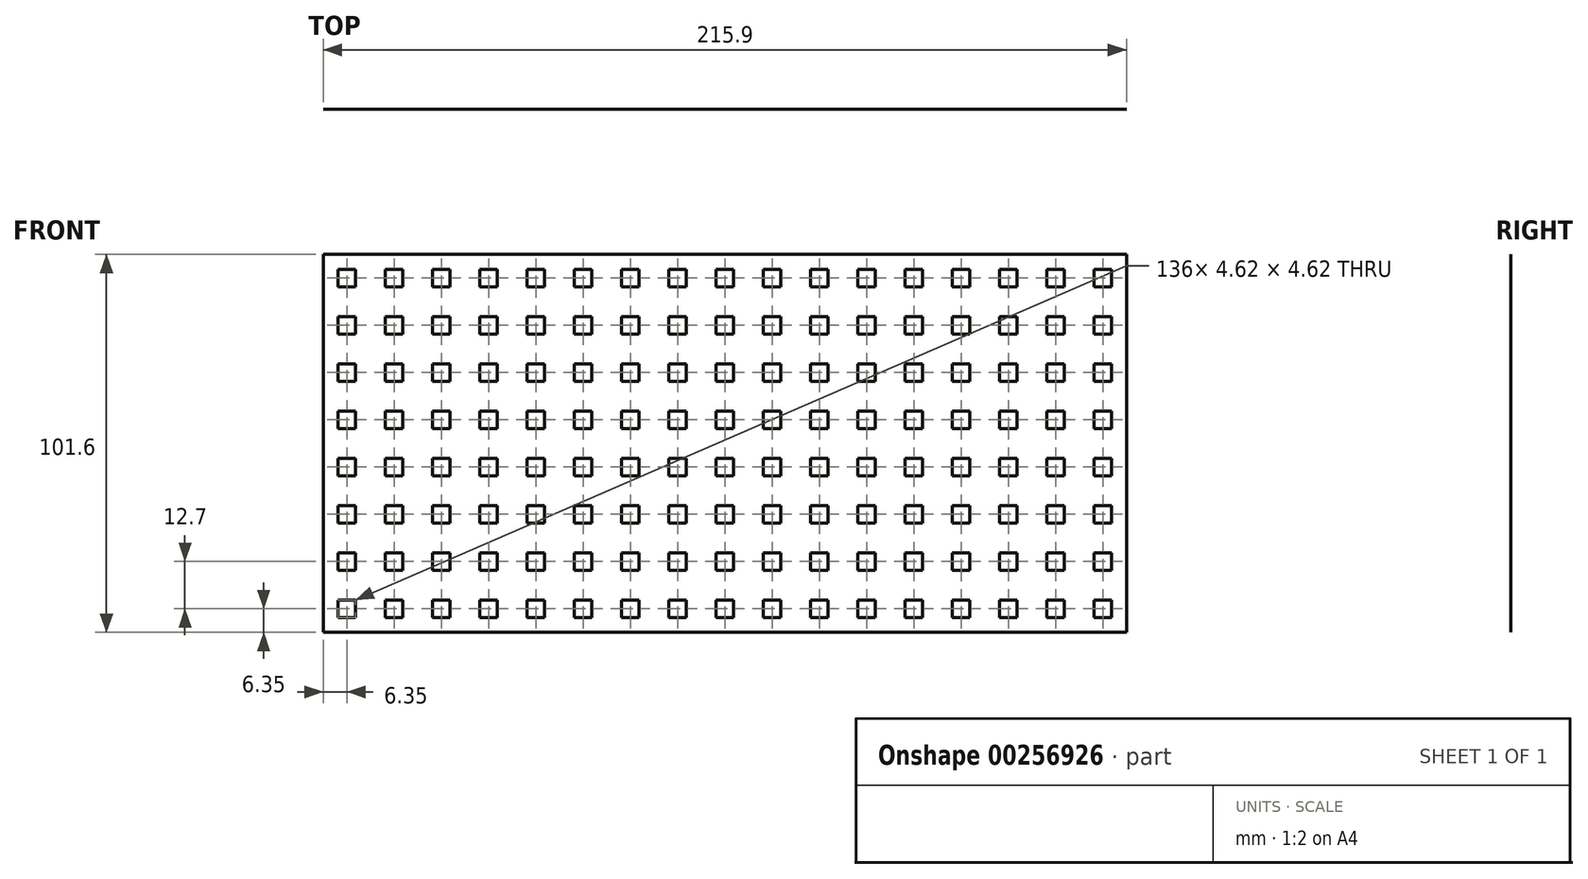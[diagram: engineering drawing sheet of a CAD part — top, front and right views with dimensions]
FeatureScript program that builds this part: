
annotation { "Feature Type Name" : "Feature", "Feature Type Description" : "" }
export const myFeature = defineFeature(function(context is Context, id is Id, definition is map)
    precondition{}
    {
        {
            var Q0;
            Q0=qCreatedBy(makeId("Front.planeOp"),FACE);
            var sketch = newSketch(context, id + "F0", { "sketchPlane" : qUnion([Q0])});
            skLineSegment(sketch, "E0.bottom", {"start": v(107.95, 50.8) * mm, "end": v(-107.95, 50.8) * mm});
            skLineSegment(sketch, "E0.top", {"start": v(107.95, -50.8) * mm, "end": v(-107.95, -50.8) * mm});
            skLineSegment(sketch, "E0.left", {"start": v(107.95, 50.8) * mm, "end": v(107.95, -50.8) * mm});
            skLineSegment(sketch, "E0.right", {"start": v(-107.95, 50.8) * mm, "end": v(-107.95, -50.8) * mm});
            skPoint(sketch, "E0.middle", {"position": v(0, 0) * mm});
            skLineSegment(sketch, "E1.bottom", {"start": v(-107.95, -50.8) * mm, "end": v(-101.6, -50.8) * mm});
            skLineSegment(sketch, "E1.left", {"start": v(-107.95, -50.8) * mm, "end": v(-107.95, -44.45) * mm});
            skLineSegment(sketch, "E2.bottom", {"start": v(-99.29, -46.76) * mm, "end": v(-103.91, -46.76) * mm});
            skLineSegment(sketch, "E2.top", {"start": v(-99.29, -42.14) * mm, "end": v(-103.91, -42.14) * mm});
            skLineSegment(sketch, "E2.left", {"start": v(-99.29, -46.76) * mm, "end": v(-99.29, -42.14) * mm});
            skLineSegment(sketch, "E2.right", {"start": v(-103.91, -46.76) * mm, "end": v(-103.91, -42.14) * mm});
            skPoint(sketch, "E2.middle", {"position": v(-101.6, -44.45) * mm});
            skLineSegment(sketch, "E3.0.1.0", {"start": v(-99.29, -29.44) * mm, "end": v(-103.91, -29.44) * mm});
            skLineSegment(sketch, "E3.0.1.1", {"start": v(-103.91, -34.06) * mm, "end": v(-103.91, -29.44) * mm});
            skLineSegment(sketch, "E3.0.1.2", {"start": v(-99.29, -34.06) * mm, "end": v(-103.91, -34.06) * mm});
            skLineSegment(sketch, "E3.0.1.3", {"start": v(-99.29, -34.06) * mm, "end": v(-99.29, -29.44) * mm});
            skLineSegment(sketch, "E3.0.2.0", {"start": v(-99.29, -16.74) * mm, "end": v(-103.91, -16.74) * mm});
            skLineSegment(sketch, "E3.0.2.1", {"start": v(-103.91, -21.36) * mm, "end": v(-103.91, -16.74) * mm});
            skLineSegment(sketch, "E3.0.2.2", {"start": v(-99.29, -21.36) * mm, "end": v(-103.91, -21.36) * mm});
            skLineSegment(sketch, "E3.0.2.3", {"start": v(-99.29, -21.36) * mm, "end": v(-99.29, -16.74) * mm});
            skLineSegment(sketch, "E3.0.3.0", {"start": v(-99.29, -4.04) * mm, "end": v(-103.91, -4.04) * mm});
            skLineSegment(sketch, "E3.0.3.1", {"start": v(-103.91, -8.66) * mm, "end": v(-103.91, -4.04) * mm});
            skLineSegment(sketch, "E3.0.3.2", {"start": v(-99.29, -8.66) * mm, "end": v(-103.91, -8.66) * mm});
            skLineSegment(sketch, "E3.0.3.3", {"start": v(-99.29, -8.66) * mm, "end": v(-99.29, -4.04) * mm});
            skLineSegment(sketch, "E3.0.4.0", {"start": v(-99.29, 8.66) * mm, "end": v(-103.91, 8.66) * mm});
            skLineSegment(sketch, "E3.0.4.1", {"start": v(-103.91, 4.04) * mm, "end": v(-103.91, 8.66) * mm});
            skLineSegment(sketch, "E3.0.4.2", {"start": v(-99.29, 4.04) * mm, "end": v(-103.91, 4.04) * mm});
            skLineSegment(sketch, "E3.0.4.3", {"start": v(-99.29, 4.04) * mm, "end": v(-99.29, 8.66) * mm});
            skLineSegment(sketch, "E3.0.5.0", {"start": v(-99.29, 21.36) * mm, "end": v(-103.91, 21.36) * mm});
            skLineSegment(sketch, "E3.0.5.1", {"start": v(-103.91, 16.74) * mm, "end": v(-103.91, 21.36) * mm});
            skLineSegment(sketch, "E3.0.5.2", {"start": v(-99.29, 16.74) * mm, "end": v(-103.91, 16.74) * mm});
            skLineSegment(sketch, "E3.0.5.3", {"start": v(-99.29, 16.74) * mm, "end": v(-99.29, 21.36) * mm});
            skLineSegment(sketch, "E3.0.6.0", {"start": v(-99.29, 34.06) * mm, "end": v(-103.91, 34.06) * mm});
            skLineSegment(sketch, "E3.0.6.1", {"start": v(-103.91, 29.44) * mm, "end": v(-103.91, 34.06) * mm});
            skLineSegment(sketch, "E3.0.6.2", {"start": v(-99.29, 29.44) * mm, "end": v(-103.91, 29.44) * mm});
            skLineSegment(sketch, "E3.0.6.3", {"start": v(-99.29, 29.44) * mm, "end": v(-99.29, 34.06) * mm});
            skLineSegment(sketch, "E3.0.7.0", {"start": v(-99.29, 46.76) * mm, "end": v(-103.91, 46.76) * mm});
            skLineSegment(sketch, "E3.0.7.1", {"start": v(-103.91, 42.14) * mm, "end": v(-103.91, 46.76) * mm});
            skLineSegment(sketch, "E3.0.7.2", {"start": v(-99.29, 42.14) * mm, "end": v(-103.91, 42.14) * mm});
            skLineSegment(sketch, "E3.0.7.3", {"start": v(-99.29, 42.14) * mm, "end": v(-99.29, 46.76) * mm});
            skLineSegment(sketch, "E3.1.0.0", {"start": v(-86.59, -42.14) * mm, "end": v(-91.21, -42.14) * mm});
            skLineSegment(sketch, "E3.1.0.1", {"start": v(-91.21, -46.76) * mm, "end": v(-91.21, -42.14) * mm});
            skLineSegment(sketch, "E3.1.0.2", {"start": v(-86.59, -46.76) * mm, "end": v(-91.21, -46.76) * mm});
            skLineSegment(sketch, "E3.1.0.3", {"start": v(-86.59, -46.76) * mm, "end": v(-86.59, -42.14) * mm});
            skLineSegment(sketch, "E3.1.1.0", {"start": v(-86.59, -29.44) * mm, "end": v(-91.21, -29.44) * mm});
            skLineSegment(sketch, "E3.1.1.1", {"start": v(-91.21, -34.06) * mm, "end": v(-91.21, -29.44) * mm});
            skLineSegment(sketch, "E3.1.1.2", {"start": v(-86.59, -34.06) * mm, "end": v(-91.21, -34.06) * mm});
            skLineSegment(sketch, "E3.1.1.3", {"start": v(-86.59, -34.06) * mm, "end": v(-86.59, -29.44) * mm});
            skLineSegment(sketch, "E3.1.2.0", {"start": v(-86.59, -16.74) * mm, "end": v(-91.21, -16.74) * mm});
            skLineSegment(sketch, "E3.1.2.1", {"start": v(-91.21, -21.36) * mm, "end": v(-91.21, -16.74) * mm});
            skLineSegment(sketch, "E3.1.2.2", {"start": v(-86.59, -21.36) * mm, "end": v(-91.21, -21.36) * mm});
            skLineSegment(sketch, "E3.1.2.3", {"start": v(-86.59, -21.36) * mm, "end": v(-86.59, -16.74) * mm});
            skLineSegment(sketch, "E3.1.3.0", {"start": v(-86.59, -4.04) * mm, "end": v(-91.21, -4.04) * mm});
            skLineSegment(sketch, "E3.1.3.1", {"start": v(-91.21, -8.66) * mm, "end": v(-91.21, -4.04) * mm});
            skLineSegment(sketch, "E3.1.3.2", {"start": v(-86.59, -8.66) * mm, "end": v(-91.21, -8.66) * mm});
            skLineSegment(sketch, "E3.1.3.3", {"start": v(-86.59, -8.66) * mm, "end": v(-86.59, -4.04) * mm});
            skLineSegment(sketch, "E3.1.4.0", {"start": v(-86.59, 8.66) * mm, "end": v(-91.21, 8.66) * mm});
            skLineSegment(sketch, "E3.1.4.1", {"start": v(-91.21, 4.04) * mm, "end": v(-91.21, 8.66) * mm});
            skLineSegment(sketch, "E3.1.4.2", {"start": v(-86.59, 4.04) * mm, "end": v(-91.21, 4.04) * mm});
            skLineSegment(sketch, "E3.1.4.3", {"start": v(-86.59, 4.04) * mm, "end": v(-86.59, 8.66) * mm});
            skLineSegment(sketch, "E3.1.5.0", {"start": v(-86.59, 21.36) * mm, "end": v(-91.21, 21.36) * mm});
            skLineSegment(sketch, "E3.1.5.1", {"start": v(-91.21, 16.74) * mm, "end": v(-91.21, 21.36) * mm});
            skLineSegment(sketch, "E3.1.5.2", {"start": v(-86.59, 16.74) * mm, "end": v(-91.21, 16.74) * mm});
            skLineSegment(sketch, "E3.1.5.3", {"start": v(-86.59, 16.74) * mm, "end": v(-86.59, 21.36) * mm});
            skLineSegment(sketch, "E3.1.6.0", {"start": v(-86.59, 34.06) * mm, "end": v(-91.21, 34.06) * mm});
            skLineSegment(sketch, "E3.1.6.1", {"start": v(-91.21, 29.44) * mm, "end": v(-91.21, 34.06) * mm});
            skLineSegment(sketch, "E3.1.6.2", {"start": v(-86.59, 29.44) * mm, "end": v(-91.21, 29.44) * mm});
            skLineSegment(sketch, "E3.1.6.3", {"start": v(-86.59, 29.44) * mm, "end": v(-86.59, 34.06) * mm});
            skLineSegment(sketch, "E3.1.7.0", {"start": v(-86.59, 46.76) * mm, "end": v(-91.21, 46.76) * mm});
            skLineSegment(sketch, "E3.1.7.1", {"start": v(-91.21, 42.14) * mm, "end": v(-91.21, 46.76) * mm});
            skLineSegment(sketch, "E3.1.7.2", {"start": v(-86.59, 42.14) * mm, "end": v(-91.21, 42.14) * mm});
            skLineSegment(sketch, "E3.1.7.3", {"start": v(-86.59, 42.14) * mm, "end": v(-86.59, 46.76) * mm});
            skLineSegment(sketch, "E3.2.0.0", {"start": v(-73.89, -42.14) * mm, "end": v(-78.51, -42.14) * mm});
            skLineSegment(sketch, "E3.2.0.1", {"start": v(-78.51, -46.76) * mm, "end": v(-78.51, -42.14) * mm});
            skLineSegment(sketch, "E3.2.0.2", {"start": v(-73.89, -46.76) * mm, "end": v(-78.51, -46.76) * mm});
            skLineSegment(sketch, "E3.2.0.3", {"start": v(-73.89, -46.76) * mm, "end": v(-73.89, -42.14) * mm});
            skLineSegment(sketch, "E3.2.1.0", {"start": v(-73.89, -29.44) * mm, "end": v(-78.51, -29.44) * mm});
            skLineSegment(sketch, "E3.2.1.1", {"start": v(-78.51, -34.06) * mm, "end": v(-78.51, -29.44) * mm});
            skLineSegment(sketch, "E3.2.1.2", {"start": v(-73.89, -34.06) * mm, "end": v(-78.51, -34.06) * mm});
            skLineSegment(sketch, "E3.2.1.3", {"start": v(-73.89, -34.06) * mm, "end": v(-73.89, -29.44) * mm});
            skLineSegment(sketch, "E3.2.2.0", {"start": v(-73.89, -16.74) * mm, "end": v(-78.51, -16.74) * mm});
            skLineSegment(sketch, "E3.2.2.1", {"start": v(-78.51, -21.36) * mm, "end": v(-78.51, -16.74) * mm});
            skLineSegment(sketch, "E3.2.2.2", {"start": v(-73.89, -21.36) * mm, "end": v(-78.51, -21.36) * mm});
            skLineSegment(sketch, "E3.2.2.3", {"start": v(-73.89, -21.36) * mm, "end": v(-73.89, -16.74) * mm});
            skLineSegment(sketch, "E3.2.3.0", {"start": v(-73.89, -4.04) * mm, "end": v(-78.51, -4.04) * mm});
            skLineSegment(sketch, "E3.2.3.1", {"start": v(-78.51, -8.66) * mm, "end": v(-78.51, -4.04) * mm});
            skLineSegment(sketch, "E3.2.3.2", {"start": v(-73.89, -8.66) * mm, "end": v(-78.51, -8.66) * mm});
            skLineSegment(sketch, "E3.2.3.3", {"start": v(-73.89, -8.66) * mm, "end": v(-73.89, -4.04) * mm});
            skLineSegment(sketch, "E3.2.4.0", {"start": v(-73.89, 8.66) * mm, "end": v(-78.51, 8.66) * mm});
            skLineSegment(sketch, "E3.2.4.1", {"start": v(-78.51, 4.04) * mm, "end": v(-78.51, 8.66) * mm});
            skLineSegment(sketch, "E3.2.4.2", {"start": v(-73.89, 4.04) * mm, "end": v(-78.51, 4.04) * mm});
            skLineSegment(sketch, "E3.2.4.3", {"start": v(-73.89, 4.04) * mm, "end": v(-73.89, 8.66) * mm});
            skLineSegment(sketch, "E3.2.5.0", {"start": v(-73.89, 21.36) * mm, "end": v(-78.51, 21.36) * mm});
            skLineSegment(sketch, "E3.2.5.1", {"start": v(-78.51, 16.74) * mm, "end": v(-78.51, 21.36) * mm});
            skLineSegment(sketch, "E3.2.5.2", {"start": v(-73.89, 16.74) * mm, "end": v(-78.51, 16.74) * mm});
            skLineSegment(sketch, "E3.2.5.3", {"start": v(-73.89, 16.74) * mm, "end": v(-73.89, 21.36) * mm});
            skLineSegment(sketch, "E3.2.6.0", {"start": v(-73.89, 34.06) * mm, "end": v(-78.51, 34.06) * mm});
            skLineSegment(sketch, "E3.2.6.1", {"start": v(-78.51, 29.44) * mm, "end": v(-78.51, 34.06) * mm});
            skLineSegment(sketch, "E3.2.6.2", {"start": v(-73.89, 29.44) * mm, "end": v(-78.51, 29.44) * mm});
            skLineSegment(sketch, "E3.2.6.3", {"start": v(-73.89, 29.44) * mm, "end": v(-73.89, 34.06) * mm});
            skLineSegment(sketch, "E3.2.7.0", {"start": v(-73.89, 46.76) * mm, "end": v(-78.51, 46.76) * mm});
            skLineSegment(sketch, "E3.2.7.1", {"start": v(-78.51, 42.14) * mm, "end": v(-78.51, 46.76) * mm});
            skLineSegment(sketch, "E3.2.7.2", {"start": v(-73.89, 42.14) * mm, "end": v(-78.51, 42.14) * mm});
            skLineSegment(sketch, "E3.2.7.3", {"start": v(-73.89, 42.14) * mm, "end": v(-73.89, 46.76) * mm});
            skLineSegment(sketch, "E3.3.0.0", {"start": v(-61.19, -42.14) * mm, "end": v(-65.81, -42.14) * mm});
            skLineSegment(sketch, "E3.3.0.1", {"start": v(-65.81, -46.76) * mm, "end": v(-65.81, -42.14) * mm});
            skLineSegment(sketch, "E3.3.0.2", {"start": v(-61.19, -46.76) * mm, "end": v(-65.81, -46.76) * mm});
            skLineSegment(sketch, "E3.3.0.3", {"start": v(-61.19, -46.76) * mm, "end": v(-61.19, -42.14) * mm});
            skLineSegment(sketch, "E3.3.1.0", {"start": v(-61.19, -29.44) * mm, "end": v(-65.81, -29.44) * mm});
            skLineSegment(sketch, "E3.3.1.1", {"start": v(-65.81, -34.06) * mm, "end": v(-65.81, -29.44) * mm});
            skLineSegment(sketch, "E3.3.1.2", {"start": v(-61.19, -34.06) * mm, "end": v(-65.81, -34.06) * mm});
            skLineSegment(sketch, "E3.3.1.3", {"start": v(-61.19, -34.06) * mm, "end": v(-61.19, -29.44) * mm});
            skLineSegment(sketch, "E3.3.2.0", {"start": v(-61.19, -16.74) * mm, "end": v(-65.81, -16.74) * mm});
            skLineSegment(sketch, "E3.3.2.1", {"start": v(-65.81, -21.36) * mm, "end": v(-65.81, -16.74) * mm});
            skLineSegment(sketch, "E3.3.2.2", {"start": v(-61.19, -21.36) * mm, "end": v(-65.81, -21.36) * mm});
            skLineSegment(sketch, "E3.3.2.3", {"start": v(-61.19, -21.36) * mm, "end": v(-61.19, -16.74) * mm});
            skLineSegment(sketch, "E3.3.3.0", {"start": v(-61.19, -4.04) * mm, "end": v(-65.81, -4.04) * mm});
            skLineSegment(sketch, "E3.3.3.1", {"start": v(-65.81, -8.66) * mm, "end": v(-65.81, -4.04) * mm});
            skLineSegment(sketch, "E3.3.3.2", {"start": v(-61.19, -8.66) * mm, "end": v(-65.81, -8.66) * mm});
            skLineSegment(sketch, "E3.3.3.3", {"start": v(-61.19, -8.66) * mm, "end": v(-61.19, -4.04) * mm});
            skLineSegment(sketch, "E3.3.4.0", {"start": v(-61.19, 8.66) * mm, "end": v(-65.81, 8.66) * mm});
            skLineSegment(sketch, "E3.3.4.1", {"start": v(-65.81, 4.04) * mm, "end": v(-65.81, 8.66) * mm});
            skLineSegment(sketch, "E3.3.4.2", {"start": v(-61.19, 4.04) * mm, "end": v(-65.81, 4.04) * mm});
            skLineSegment(sketch, "E3.3.4.3", {"start": v(-61.19, 4.04) * mm, "end": v(-61.19, 8.66) * mm});
            skLineSegment(sketch, "E3.3.5.0", {"start": v(-61.19, 21.36) * mm, "end": v(-65.81, 21.36) * mm});
            skLineSegment(sketch, "E3.3.5.1", {"start": v(-65.81, 16.74) * mm, "end": v(-65.81, 21.36) * mm});
            skLineSegment(sketch, "E3.3.5.2", {"start": v(-61.19, 16.74) * mm, "end": v(-65.81, 16.74) * mm});
            skLineSegment(sketch, "E3.3.5.3", {"start": v(-61.19, 16.74) * mm, "end": v(-61.19, 21.36) * mm});
            skLineSegment(sketch, "E3.3.6.0", {"start": v(-61.19, 34.06) * mm, "end": v(-65.81, 34.06) * mm});
            skLineSegment(sketch, "E3.3.6.1", {"start": v(-65.81, 29.44) * mm, "end": v(-65.81, 34.06) * mm});
            skLineSegment(sketch, "E3.3.6.2", {"start": v(-61.19, 29.44) * mm, "end": v(-65.81, 29.44) * mm});
            skLineSegment(sketch, "E3.3.6.3", {"start": v(-61.19, 29.44) * mm, "end": v(-61.19, 34.06) * mm});
            skLineSegment(sketch, "E3.3.7.0", {"start": v(-61.19, 46.76) * mm, "end": v(-65.81, 46.76) * mm});
            skLineSegment(sketch, "E3.3.7.1", {"start": v(-65.81, 42.14) * mm, "end": v(-65.81, 46.76) * mm});
            skLineSegment(sketch, "E3.3.7.2", {"start": v(-61.19, 42.14) * mm, "end": v(-65.81, 42.14) * mm});
            skLineSegment(sketch, "E3.3.7.3", {"start": v(-61.19, 42.14) * mm, "end": v(-61.19, 46.76) * mm});
            skLineSegment(sketch, "E3.4.0.0", {"start": v(-48.49, -42.14) * mm, "end": v(-53.11, -42.14) * mm});
            skLineSegment(sketch, "E3.4.0.1", {"start": v(-53.11, -46.76) * mm, "end": v(-53.11, -42.14) * mm});
            skLineSegment(sketch, "E3.4.0.2", {"start": v(-48.49, -46.76) * mm, "end": v(-53.11, -46.76) * mm});
            skLineSegment(sketch, "E3.4.0.3", {"start": v(-48.49, -46.76) * mm, "end": v(-48.49, -42.14) * mm});
            skLineSegment(sketch, "E3.4.1.0", {"start": v(-48.49, -29.44) * mm, "end": v(-53.11, -29.44) * mm});
            skLineSegment(sketch, "E3.4.1.1", {"start": v(-53.11, -34.06) * mm, "end": v(-53.11, -29.44) * mm});
            skLineSegment(sketch, "E3.4.1.2", {"start": v(-48.49, -34.06) * mm, "end": v(-53.11, -34.06) * mm});
            skLineSegment(sketch, "E3.4.1.3", {"start": v(-48.49, -34.06) * mm, "end": v(-48.49, -29.44) * mm});
            skLineSegment(sketch, "E3.4.2.0", {"start": v(-48.49, -16.74) * mm, "end": v(-53.11, -16.74) * mm});
            skLineSegment(sketch, "E3.4.2.1", {"start": v(-53.11, -21.36) * mm, "end": v(-53.11, -16.74) * mm});
            skLineSegment(sketch, "E3.4.2.2", {"start": v(-48.49, -21.36) * mm, "end": v(-53.11, -21.36) * mm});
            skLineSegment(sketch, "E3.4.2.3", {"start": v(-48.49, -21.36) * mm, "end": v(-48.49, -16.74) * mm});
            skLineSegment(sketch, "E3.4.3.0", {"start": v(-48.49, -4.04) * mm, "end": v(-53.11, -4.04) * mm});
            skLineSegment(sketch, "E3.4.3.1", {"start": v(-53.11, -8.66) * mm, "end": v(-53.11, -4.04) * mm});
            skLineSegment(sketch, "E3.4.3.2", {"start": v(-48.49, -8.66) * mm, "end": v(-53.11, -8.66) * mm});
            skLineSegment(sketch, "E3.4.3.3", {"start": v(-48.49, -8.66) * mm, "end": v(-48.49, -4.04) * mm});
            skLineSegment(sketch, "E3.4.4.0", {"start": v(-48.49, 8.66) * mm, "end": v(-53.11, 8.66) * mm});
            skLineSegment(sketch, "E3.4.4.1", {"start": v(-53.11, 4.04) * mm, "end": v(-53.11, 8.66) * mm});
            skLineSegment(sketch, "E3.4.4.2", {"start": v(-48.49, 4.04) * mm, "end": v(-53.11, 4.04) * mm});
            skLineSegment(sketch, "E3.4.4.3", {"start": v(-48.49, 4.04) * mm, "end": v(-48.49, 8.66) * mm});
            skLineSegment(sketch, "E3.4.5.0", {"start": v(-48.49, 21.36) * mm, "end": v(-53.11, 21.36) * mm});
            skLineSegment(sketch, "E3.4.5.1", {"start": v(-53.11, 16.74) * mm, "end": v(-53.11, 21.36) * mm});
            skLineSegment(sketch, "E3.4.5.2", {"start": v(-48.49, 16.74) * mm, "end": v(-53.11, 16.74) * mm});
            skLineSegment(sketch, "E3.4.5.3", {"start": v(-48.49, 16.74) * mm, "end": v(-48.49, 21.36) * mm});
            skLineSegment(sketch, "E3.4.6.0", {"start": v(-48.49, 34.06) * mm, "end": v(-53.11, 34.06) * mm});
            skLineSegment(sketch, "E3.4.6.1", {"start": v(-53.11, 29.44) * mm, "end": v(-53.11, 34.06) * mm});
            skLineSegment(sketch, "E3.4.6.2", {"start": v(-48.49, 29.44) * mm, "end": v(-53.11, 29.44) * mm});
            skLineSegment(sketch, "E3.4.6.3", {"start": v(-48.49, 29.44) * mm, "end": v(-48.49, 34.06) * mm});
            skLineSegment(sketch, "E3.4.7.0", {"start": v(-48.49, 46.76) * mm, "end": v(-53.11, 46.76) * mm});
            skLineSegment(sketch, "E3.4.7.1", {"start": v(-53.11, 42.14) * mm, "end": v(-53.11, 46.76) * mm});
            skLineSegment(sketch, "E3.4.7.2", {"start": v(-48.49, 42.14) * mm, "end": v(-53.11, 42.14) * mm});
            skLineSegment(sketch, "E3.4.7.3", {"start": v(-48.49, 42.14) * mm, "end": v(-48.49, 46.76) * mm});
            skLineSegment(sketch, "E3.5.0.0", {"start": v(-35.79, -42.14) * mm, "end": v(-40.41, -42.14) * mm});
            skLineSegment(sketch, "E3.5.0.1", {"start": v(-40.41, -46.76) * mm, "end": v(-40.41, -42.14) * mm});
            skLineSegment(sketch, "E3.5.0.2", {"start": v(-35.79, -46.76) * mm, "end": v(-40.41, -46.76) * mm});
            skLineSegment(sketch, "E3.5.0.3", {"start": v(-35.79, -46.76) * mm, "end": v(-35.79, -42.14) * mm});
            skLineSegment(sketch, "E3.5.1.0", {"start": v(-35.79, -29.44) * mm, "end": v(-40.41, -29.44) * mm});
            skLineSegment(sketch, "E3.5.1.1", {"start": v(-40.41, -34.06) * mm, "end": v(-40.41, -29.44) * mm});
            skLineSegment(sketch, "E3.5.1.2", {"start": v(-35.79, -34.06) * mm, "end": v(-40.41, -34.06) * mm});
            skLineSegment(sketch, "E3.5.1.3", {"start": v(-35.79, -34.06) * mm, "end": v(-35.79, -29.44) * mm});
            skLineSegment(sketch, "E3.5.2.0", {"start": v(-35.79, -16.74) * mm, "end": v(-40.41, -16.74) * mm});
            skLineSegment(sketch, "E3.5.2.1", {"start": v(-40.41, -21.36) * mm, "end": v(-40.41, -16.74) * mm});
            skLineSegment(sketch, "E3.5.2.2", {"start": v(-35.79, -21.36) * mm, "end": v(-40.41, -21.36) * mm});
            skLineSegment(sketch, "E3.5.2.3", {"start": v(-35.79, -21.36) * mm, "end": v(-35.79, -16.74) * mm});
            skLineSegment(sketch, "E3.5.3.0", {"start": v(-35.79, -4.04) * mm, "end": v(-40.41, -4.04) * mm});
            skLineSegment(sketch, "E3.5.3.1", {"start": v(-40.41, -8.66) * mm, "end": v(-40.41, -4.04) * mm});
            skLineSegment(sketch, "E3.5.3.2", {"start": v(-35.79, -8.66) * mm, "end": v(-40.41, -8.66) * mm});
            skLineSegment(sketch, "E3.5.3.3", {"start": v(-35.79, -8.66) * mm, "end": v(-35.79, -4.04) * mm});
            skLineSegment(sketch, "E3.5.4.0", {"start": v(-35.79, 8.66) * mm, "end": v(-40.41, 8.66) * mm});
            skLineSegment(sketch, "E3.5.4.1", {"start": v(-40.41, 4.04) * mm, "end": v(-40.41, 8.66) * mm});
            skLineSegment(sketch, "E3.5.4.2", {"start": v(-35.79, 4.04) * mm, "end": v(-40.41, 4.04) * mm});
            skLineSegment(sketch, "E3.5.4.3", {"start": v(-35.79, 4.04) * mm, "end": v(-35.79, 8.66) * mm});
            skLineSegment(sketch, "E3.5.5.0", {"start": v(-35.79, 21.36) * mm, "end": v(-40.41, 21.36) * mm});
            skLineSegment(sketch, "E3.5.5.1", {"start": v(-40.41, 16.74) * mm, "end": v(-40.41, 21.36) * mm});
            skLineSegment(sketch, "E3.5.5.2", {"start": v(-35.79, 16.74) * mm, "end": v(-40.41, 16.74) * mm});
            skLineSegment(sketch, "E3.5.5.3", {"start": v(-35.79, 16.74) * mm, "end": v(-35.79, 21.36) * mm});
            skLineSegment(sketch, "E3.5.6.0", {"start": v(-35.79, 34.06) * mm, "end": v(-40.41, 34.06) * mm});
            skLineSegment(sketch, "E3.5.6.1", {"start": v(-40.41, 29.44) * mm, "end": v(-40.41, 34.06) * mm});
            skLineSegment(sketch, "E3.5.6.2", {"start": v(-35.79, 29.44) * mm, "end": v(-40.41, 29.44) * mm});
            skLineSegment(sketch, "E3.5.6.3", {"start": v(-35.79, 29.44) * mm, "end": v(-35.79, 34.06) * mm});
            skLineSegment(sketch, "E3.5.7.0", {"start": v(-35.79, 46.76) * mm, "end": v(-40.41, 46.76) * mm});
            skLineSegment(sketch, "E3.5.7.1", {"start": v(-40.41, 42.14) * mm, "end": v(-40.41, 46.76) * mm});
            skLineSegment(sketch, "E3.5.7.2", {"start": v(-35.79, 42.14) * mm, "end": v(-40.41, 42.14) * mm});
            skLineSegment(sketch, "E3.5.7.3", {"start": v(-35.79, 42.14) * mm, "end": v(-35.79, 46.76) * mm});
            skLineSegment(sketch, "E3.6.0.0", {"start": v(-23.09, -42.14) * mm, "end": v(-27.71, -42.14) * mm});
            skLineSegment(sketch, "E3.6.0.1", {"start": v(-27.71, -46.76) * mm, "end": v(-27.71, -42.14) * mm});
            skLineSegment(sketch, "E3.6.0.2", {"start": v(-23.09, -46.76) * mm, "end": v(-27.71, -46.76) * mm});
            skLineSegment(sketch, "E3.6.0.3", {"start": v(-23.09, -46.76) * mm, "end": v(-23.09, -42.14) * mm});
            skLineSegment(sketch, "E3.6.1.0", {"start": v(-23.09, -29.44) * mm, "end": v(-27.71, -29.44) * mm});
            skLineSegment(sketch, "E3.6.1.1", {"start": v(-27.71, -34.06) * mm, "end": v(-27.71, -29.44) * mm});
            skLineSegment(sketch, "E3.6.1.2", {"start": v(-23.09, -34.06) * mm, "end": v(-27.71, -34.06) * mm});
            skLineSegment(sketch, "E3.6.1.3", {"start": v(-23.09, -34.06) * mm, "end": v(-23.09, -29.44) * mm});
            skLineSegment(sketch, "E3.6.2.0", {"start": v(-23.09, -16.74) * mm, "end": v(-27.71, -16.74) * mm});
            skLineSegment(sketch, "E3.6.2.1", {"start": v(-27.71, -21.36) * mm, "end": v(-27.71, -16.74) * mm});
            skLineSegment(sketch, "E3.6.2.2", {"start": v(-23.09, -21.36) * mm, "end": v(-27.71, -21.36) * mm});
            skLineSegment(sketch, "E3.6.2.3", {"start": v(-23.09, -21.36) * mm, "end": v(-23.09, -16.74) * mm});
            skLineSegment(sketch, "E3.6.3.0", {"start": v(-23.09, -4.04) * mm, "end": v(-27.71, -4.04) * mm});
            skLineSegment(sketch, "E3.6.3.1", {"start": v(-27.71, -8.66) * mm, "end": v(-27.71, -4.04) * mm});
            skLineSegment(sketch, "E3.6.3.2", {"start": v(-23.09, -8.66) * mm, "end": v(-27.71, -8.66) * mm});
            skLineSegment(sketch, "E3.6.3.3", {"start": v(-23.09, -8.66) * mm, "end": v(-23.09, -4.04) * mm});
            skLineSegment(sketch, "E3.6.4.0", {"start": v(-23.09, 8.66) * mm, "end": v(-27.71, 8.66) * mm});
            skLineSegment(sketch, "E3.6.4.1", {"start": v(-27.71, 4.04) * mm, "end": v(-27.71, 8.66) * mm});
            skLineSegment(sketch, "E3.6.4.2", {"start": v(-23.09, 4.04) * mm, "end": v(-27.71, 4.04) * mm});
            skLineSegment(sketch, "E3.6.4.3", {"start": v(-23.09, 4.04) * mm, "end": v(-23.09, 8.66) * mm});
            skLineSegment(sketch, "E3.6.5.0", {"start": v(-23.09, 21.36) * mm, "end": v(-27.71, 21.36) * mm});
            skLineSegment(sketch, "E3.6.5.1", {"start": v(-27.71, 16.74) * mm, "end": v(-27.71, 21.36) * mm});
            skLineSegment(sketch, "E3.6.5.2", {"start": v(-23.09, 16.74) * mm, "end": v(-27.71, 16.74) * mm});
            skLineSegment(sketch, "E3.6.5.3", {"start": v(-23.09, 16.74) * mm, "end": v(-23.09, 21.36) * mm});
            skLineSegment(sketch, "E3.6.6.0", {"start": v(-23.09, 34.06) * mm, "end": v(-27.71, 34.06) * mm});
            skLineSegment(sketch, "E3.6.6.1", {"start": v(-27.71, 29.44) * mm, "end": v(-27.71, 34.06) * mm});
            skLineSegment(sketch, "E3.6.6.2", {"start": v(-23.09, 29.44) * mm, "end": v(-27.71, 29.44) * mm});
            skLineSegment(sketch, "E3.6.6.3", {"start": v(-23.09, 29.44) * mm, "end": v(-23.09, 34.06) * mm});
            skLineSegment(sketch, "E3.6.7.0", {"start": v(-23.09, 46.76) * mm, "end": v(-27.71, 46.76) * mm});
            skLineSegment(sketch, "E3.6.7.1", {"start": v(-27.71, 42.14) * mm, "end": v(-27.71, 46.76) * mm});
            skLineSegment(sketch, "E3.6.7.2", {"start": v(-23.09, 42.14) * mm, "end": v(-27.71, 42.14) * mm});
            skLineSegment(sketch, "E3.6.7.3", {"start": v(-23.09, 42.14) * mm, "end": v(-23.09, 46.76) * mm});
            skLineSegment(sketch, "E3.7.0.0", {"start": v(-10.39, -42.14) * mm, "end": v(-15.01, -42.14) * mm});
            skLineSegment(sketch, "E3.7.0.1", {"start": v(-15.01, -46.76) * mm, "end": v(-15.01, -42.14) * mm});
            skLineSegment(sketch, "E3.7.0.2", {"start": v(-10.39, -46.76) * mm, "end": v(-15.01, -46.76) * mm});
            skLineSegment(sketch, "E3.7.0.3", {"start": v(-10.39, -46.76) * mm, "end": v(-10.39, -42.14) * mm});
            skLineSegment(sketch, "E3.7.1.0", {"start": v(-10.39, -29.44) * mm, "end": v(-15.01, -29.44) * mm});
            skLineSegment(sketch, "E3.7.1.1", {"start": v(-15.01, -34.06) * mm, "end": v(-15.01, -29.44) * mm});
            skLineSegment(sketch, "E3.7.1.2", {"start": v(-10.39, -34.06) * mm, "end": v(-15.01, -34.06) * mm});
            skLineSegment(sketch, "E3.7.1.3", {"start": v(-10.39, -34.06) * mm, "end": v(-10.39, -29.44) * mm});
            skLineSegment(sketch, "E3.7.2.0", {"start": v(-10.39, -16.74) * mm, "end": v(-15.01, -16.74) * mm});
            skLineSegment(sketch, "E3.7.2.1", {"start": v(-15.01, -21.36) * mm, "end": v(-15.01, -16.74) * mm});
            skLineSegment(sketch, "E3.7.2.2", {"start": v(-10.39, -21.36) * mm, "end": v(-15.01, -21.36) * mm});
            skLineSegment(sketch, "E3.7.2.3", {"start": v(-10.39, -21.36) * mm, "end": v(-10.39, -16.74) * mm});
            skLineSegment(sketch, "E3.7.3.0", {"start": v(-10.39, -4.04) * mm, "end": v(-15.01, -4.04) * mm});
            skLineSegment(sketch, "E3.7.3.1", {"start": v(-15.01, -8.66) * mm, "end": v(-15.01, -4.04) * mm});
            skLineSegment(sketch, "E3.7.3.2", {"start": v(-10.39, -8.66) * mm, "end": v(-15.01, -8.66) * mm});
            skLineSegment(sketch, "E3.7.3.3", {"start": v(-10.39, -8.66) * mm, "end": v(-10.39, -4.04) * mm});
            skLineSegment(sketch, "E3.7.4.0", {"start": v(-10.39, 8.66) * mm, "end": v(-15.01, 8.66) * mm});
            skLineSegment(sketch, "E3.7.4.1", {"start": v(-15.01, 4.04) * mm, "end": v(-15.01, 8.66) * mm});
            skLineSegment(sketch, "E3.7.4.2", {"start": v(-10.39, 4.04) * mm, "end": v(-15.01, 4.04) * mm});
            skLineSegment(sketch, "E3.7.4.3", {"start": v(-10.39, 4.04) * mm, "end": v(-10.39, 8.66) * mm});
            skLineSegment(sketch, "E3.7.5.0", {"start": v(-10.39, 21.36) * mm, "end": v(-15.01, 21.36) * mm});
            skLineSegment(sketch, "E3.7.5.1", {"start": v(-15.01, 16.74) * mm, "end": v(-15.01, 21.36) * mm});
            skLineSegment(sketch, "E3.7.5.2", {"start": v(-10.39, 16.74) * mm, "end": v(-15.01, 16.74) * mm});
            skLineSegment(sketch, "E3.7.5.3", {"start": v(-10.39, 16.74) * mm, "end": v(-10.39, 21.36) * mm});
            skLineSegment(sketch, "E3.7.6.0", {"start": v(-10.39, 34.06) * mm, "end": v(-15.01, 34.06) * mm});
            skLineSegment(sketch, "E3.7.6.1", {"start": v(-15.01, 29.44) * mm, "end": v(-15.01, 34.06) * mm});
            skLineSegment(sketch, "E3.7.6.2", {"start": v(-10.39, 29.44) * mm, "end": v(-15.01, 29.44) * mm});
            skLineSegment(sketch, "E3.7.6.3", {"start": v(-10.39, 29.44) * mm, "end": v(-10.39, 34.06) * mm});
            skLineSegment(sketch, "E3.7.7.0", {"start": v(-10.39, 46.76) * mm, "end": v(-15.01, 46.76) * mm});
            skLineSegment(sketch, "E3.7.7.1", {"start": v(-15.01, 42.14) * mm, "end": v(-15.01, 46.76) * mm});
            skLineSegment(sketch, "E3.7.7.2", {"start": v(-10.39, 42.14) * mm, "end": v(-15.01, 42.14) * mm});
            skLineSegment(sketch, "E3.7.7.3", {"start": v(-10.39, 42.14) * mm, "end": v(-10.39, 46.76) * mm});
            skLineSegment(sketch, "E3.8.0.0", {"start": v(2.31, -42.14) * mm, "end": v(-2.31, -42.14) * mm});
            skLineSegment(sketch, "E3.8.0.1", {"start": v(-2.31, -46.76) * mm, "end": v(-2.31, -42.14) * mm});
            skLineSegment(sketch, "E3.8.0.2", {"start": v(2.31, -46.76) * mm, "end": v(-2.31, -46.76) * mm});
            skLineSegment(sketch, "E3.8.0.3", {"start": v(2.31, -46.76) * mm, "end": v(2.31, -42.14) * mm});
            skLineSegment(sketch, "E3.8.1.0", {"start": v(2.31, -29.44) * mm, "end": v(-2.31, -29.44) * mm});
            skLineSegment(sketch, "E3.8.1.1", {"start": v(-2.31, -34.06) * mm, "end": v(-2.31, -29.44) * mm});
            skLineSegment(sketch, "E3.8.1.2", {"start": v(2.31, -34.06) * mm, "end": v(-2.31, -34.06) * mm});
            skLineSegment(sketch, "E3.8.1.3", {"start": v(2.31, -34.06) * mm, "end": v(2.31, -29.44) * mm});
            skLineSegment(sketch, "E3.8.2.0", {"start": v(2.31, -16.74) * mm, "end": v(-2.31, -16.74) * mm});
            skLineSegment(sketch, "E3.8.2.1", {"start": v(-2.31, -21.36) * mm, "end": v(-2.31, -16.74) * mm});
            skLineSegment(sketch, "E3.8.2.2", {"start": v(2.31, -21.36) * mm, "end": v(-2.31, -21.36) * mm});
            skLineSegment(sketch, "E3.8.2.3", {"start": v(2.31, -21.36) * mm, "end": v(2.31, -16.74) * mm});
            skLineSegment(sketch, "E3.8.3.0", {"start": v(2.31, -4.04) * mm, "end": v(-2.31, -4.04) * mm});
            skLineSegment(sketch, "E3.8.3.1", {"start": v(-2.31, -8.66) * mm, "end": v(-2.31, -4.04) * mm});
            skLineSegment(sketch, "E3.8.3.2", {"start": v(2.31, -8.66) * mm, "end": v(-2.31, -8.66) * mm});
            skLineSegment(sketch, "E3.8.3.3", {"start": v(2.31, -8.66) * mm, "end": v(2.31, -4.04) * mm});
            skLineSegment(sketch, "E3.8.4.0", {"start": v(2.31, 8.66) * mm, "end": v(-2.31, 8.66) * mm});
            skLineSegment(sketch, "E3.8.4.1", {"start": v(-2.31, 4.04) * mm, "end": v(-2.31, 8.66) * mm});
            skLineSegment(sketch, "E3.8.4.2", {"start": v(2.31, 4.04) * mm, "end": v(-2.31, 4.04) * mm});
            skLineSegment(sketch, "E3.8.4.3", {"start": v(2.31, 4.04) * mm, "end": v(2.31, 8.66) * mm});
            skLineSegment(sketch, "E3.8.5.0", {"start": v(2.31, 21.36) * mm, "end": v(-2.31, 21.36) * mm});
            skLineSegment(sketch, "E3.8.5.1", {"start": v(-2.31, 16.74) * mm, "end": v(-2.31, 21.36) * mm});
            skLineSegment(sketch, "E3.8.5.2", {"start": v(2.31, 16.74) * mm, "end": v(-2.31, 16.74) * mm});
            skLineSegment(sketch, "E3.8.5.3", {"start": v(2.31, 16.74) * mm, "end": v(2.31, 21.36) * mm});
            skLineSegment(sketch, "E3.8.6.0", {"start": v(2.31, 34.06) * mm, "end": v(-2.31, 34.06) * mm});
            skLineSegment(sketch, "E3.8.6.1", {"start": v(-2.31, 29.44) * mm, "end": v(-2.31, 34.06) * mm});
            skLineSegment(sketch, "E3.8.6.2", {"start": v(2.31, 29.44) * mm, "end": v(-2.31, 29.44) * mm});
            skLineSegment(sketch, "E3.8.6.3", {"start": v(2.31, 29.44) * mm, "end": v(2.31, 34.06) * mm});
            skLineSegment(sketch, "E3.8.7.0", {"start": v(2.31, 46.76) * mm, "end": v(-2.31, 46.76) * mm});
            skLineSegment(sketch, "E3.8.7.1", {"start": v(-2.31, 42.14) * mm, "end": v(-2.31, 46.76) * mm});
            skLineSegment(sketch, "E3.8.7.2", {"start": v(2.31, 42.14) * mm, "end": v(-2.31, 42.14) * mm});
            skLineSegment(sketch, "E3.8.7.3", {"start": v(2.31, 42.14) * mm, "end": v(2.31, 46.76) * mm});
            skLineSegment(sketch, "E3.9.0.0", {"start": v(15.01, -42.14) * mm, "end": v(10.39, -42.14) * mm});
            skLineSegment(sketch, "E3.9.0.1", {"start": v(10.39, -46.76) * mm, "end": v(10.39, -42.14) * mm});
            skLineSegment(sketch, "E3.9.0.2", {"start": v(15.01, -46.76) * mm, "end": v(10.39, -46.76) * mm});
            skLineSegment(sketch, "E3.9.0.3", {"start": v(15.01, -46.76) * mm, "end": v(15.01, -42.14) * mm});
            skLineSegment(sketch, "E3.9.1.0", {"start": v(15.01, -29.44) * mm, "end": v(10.39, -29.44) * mm});
            skLineSegment(sketch, "E3.9.1.1", {"start": v(10.39, -34.06) * mm, "end": v(10.39, -29.44) * mm});
            skLineSegment(sketch, "E3.9.1.2", {"start": v(15.01, -34.06) * mm, "end": v(10.39, -34.06) * mm});
            skLineSegment(sketch, "E3.9.1.3", {"start": v(15.01, -34.06) * mm, "end": v(15.01, -29.44) * mm});
            skLineSegment(sketch, "E3.9.2.0", {"start": v(15.01, -16.74) * mm, "end": v(10.39, -16.74) * mm});
            skLineSegment(sketch, "E3.9.2.1", {"start": v(10.39, -21.36) * mm, "end": v(10.39, -16.74) * mm});
            skLineSegment(sketch, "E3.9.2.2", {"start": v(15.01, -21.36) * mm, "end": v(10.39, -21.36) * mm});
            skLineSegment(sketch, "E3.9.2.3", {"start": v(15.01, -21.36) * mm, "end": v(15.01, -16.74) * mm});
            skLineSegment(sketch, "E3.9.3.0", {"start": v(15.01, -4.04) * mm, "end": v(10.39, -4.04) * mm});
            skLineSegment(sketch, "E3.9.3.1", {"start": v(10.39, -8.66) * mm, "end": v(10.39, -4.04) * mm});
            skLineSegment(sketch, "E3.9.3.2", {"start": v(15.01, -8.66) * mm, "end": v(10.39, -8.66) * mm});
            skLineSegment(sketch, "E3.9.3.3", {"start": v(15.01, -8.66) * mm, "end": v(15.01, -4.04) * mm});
            skLineSegment(sketch, "E3.9.4.0", {"start": v(15.01, 8.66) * mm, "end": v(10.39, 8.66) * mm});
            skLineSegment(sketch, "E3.9.4.1", {"start": v(10.39, 4.04) * mm, "end": v(10.39, 8.66) * mm});
            skLineSegment(sketch, "E3.9.4.2", {"start": v(15.01, 4.04) * mm, "end": v(10.39, 4.04) * mm});
            skLineSegment(sketch, "E3.9.4.3", {"start": v(15.01, 4.04) * mm, "end": v(15.01, 8.66) * mm});
            skLineSegment(sketch, "E3.9.5.0", {"start": v(15.01, 21.36) * mm, "end": v(10.39, 21.36) * mm});
            skLineSegment(sketch, "E3.9.5.1", {"start": v(10.39, 16.74) * mm, "end": v(10.39, 21.36) * mm});
            skLineSegment(sketch, "E3.9.5.2", {"start": v(15.01, 16.74) * mm, "end": v(10.39, 16.74) * mm});
            skLineSegment(sketch, "E3.9.5.3", {"start": v(15.01, 16.74) * mm, "end": v(15.01, 21.36) * mm});
            skLineSegment(sketch, "E3.9.6.0", {"start": v(15.01, 34.06) * mm, "end": v(10.39, 34.06) * mm});
            skLineSegment(sketch, "E3.9.6.1", {"start": v(10.39, 29.44) * mm, "end": v(10.39, 34.06) * mm});
            skLineSegment(sketch, "E3.9.6.2", {"start": v(15.01, 29.44) * mm, "end": v(10.39, 29.44) * mm});
            skLineSegment(sketch, "E3.9.6.3", {"start": v(15.01, 29.44) * mm, "end": v(15.01, 34.06) * mm});
            skLineSegment(sketch, "E3.9.7.0", {"start": v(15.01, 46.76) * mm, "end": v(10.39, 46.76) * mm});
            skLineSegment(sketch, "E3.9.7.1", {"start": v(10.39, 42.14) * mm, "end": v(10.39, 46.76) * mm});
            skLineSegment(sketch, "E3.9.7.2", {"start": v(15.01, 42.14) * mm, "end": v(10.39, 42.14) * mm});
            skLineSegment(sketch, "E3.9.7.3", {"start": v(15.01, 42.14) * mm, "end": v(15.01, 46.76) * mm});
            skLineSegment(sketch, "E3.10.0.0", {"start": v(27.71, -42.14) * mm, "end": v(23.09, -42.14) * mm});
            skLineSegment(sketch, "E3.10.0.1", {"start": v(23.09, -46.76) * mm, "end": v(23.09, -42.14) * mm});
            skLineSegment(sketch, "E3.10.0.2", {"start": v(27.71, -46.76) * mm, "end": v(23.09, -46.76) * mm});
            skLineSegment(sketch, "E3.10.0.3", {"start": v(27.71, -46.76) * mm, "end": v(27.71, -42.14) * mm});
            skLineSegment(sketch, "E3.10.1.0", {"start": v(27.71, -29.44) * mm, "end": v(23.09, -29.44) * mm});
            skLineSegment(sketch, "E3.10.1.1", {"start": v(23.09, -34.06) * mm, "end": v(23.09, -29.44) * mm});
            skLineSegment(sketch, "E3.10.1.2", {"start": v(27.71, -34.06) * mm, "end": v(23.09, -34.06) * mm});
            skLineSegment(sketch, "E3.10.1.3", {"start": v(27.71, -34.06) * mm, "end": v(27.71, -29.44) * mm});
            skLineSegment(sketch, "E3.10.2.0", {"start": v(27.71, -16.74) * mm, "end": v(23.09, -16.74) * mm});
            skLineSegment(sketch, "E3.10.2.1", {"start": v(23.09, -21.36) * mm, "end": v(23.09, -16.74) * mm});
            skLineSegment(sketch, "E3.10.2.2", {"start": v(27.71, -21.36) * mm, "end": v(23.09, -21.36) * mm});
            skLineSegment(sketch, "E3.10.2.3", {"start": v(27.71, -21.36) * mm, "end": v(27.71, -16.74) * mm});
            skLineSegment(sketch, "E3.10.3.0", {"start": v(27.71, -4.04) * mm, "end": v(23.09, -4.04) * mm});
            skLineSegment(sketch, "E3.10.3.1", {"start": v(23.09, -8.66) * mm, "end": v(23.09, -4.04) * mm});
            skLineSegment(sketch, "E3.10.3.2", {"start": v(27.71, -8.66) * mm, "end": v(23.09, -8.66) * mm});
            skLineSegment(sketch, "E3.10.3.3", {"start": v(27.71, -8.66) * mm, "end": v(27.71, -4.04) * mm});
            skLineSegment(sketch, "E3.10.4.0", {"start": v(27.71, 8.66) * mm, "end": v(23.09, 8.66) * mm});
            skLineSegment(sketch, "E3.10.4.1", {"start": v(23.09, 4.04) * mm, "end": v(23.09, 8.66) * mm});
            skLineSegment(sketch, "E3.10.4.2", {"start": v(27.71, 4.04) * mm, "end": v(23.09, 4.04) * mm});
            skLineSegment(sketch, "E3.10.4.3", {"start": v(27.71, 4.04) * mm, "end": v(27.71, 8.66) * mm});
            skLineSegment(sketch, "E3.10.5.0", {"start": v(27.71, 21.36) * mm, "end": v(23.09, 21.36) * mm});
            skLineSegment(sketch, "E3.10.5.1", {"start": v(23.09, 16.74) * mm, "end": v(23.09, 21.36) * mm});
            skLineSegment(sketch, "E3.10.5.2", {"start": v(27.71, 16.74) * mm, "end": v(23.09, 16.74) * mm});
            skLineSegment(sketch, "E3.10.5.3", {"start": v(27.71, 16.74) * mm, "end": v(27.71, 21.36) * mm});
            skLineSegment(sketch, "E3.10.6.0", {"start": v(27.71, 34.06) * mm, "end": v(23.09, 34.06) * mm});
            skLineSegment(sketch, "E3.10.6.1", {"start": v(23.09, 29.44) * mm, "end": v(23.09, 34.06) * mm});
            skLineSegment(sketch, "E3.10.6.2", {"start": v(27.71, 29.44) * mm, "end": v(23.09, 29.44) * mm});
            skLineSegment(sketch, "E3.10.6.3", {"start": v(27.71, 29.44) * mm, "end": v(27.71, 34.06) * mm});
            skLineSegment(sketch, "E3.10.7.0", {"start": v(27.71, 46.76) * mm, "end": v(23.09, 46.76) * mm});
            skLineSegment(sketch, "E3.10.7.1", {"start": v(23.09, 42.14) * mm, "end": v(23.09, 46.76) * mm});
            skLineSegment(sketch, "E3.10.7.2", {"start": v(27.71, 42.14) * mm, "end": v(23.09, 42.14) * mm});
            skLineSegment(sketch, "E3.10.7.3", {"start": v(27.71, 42.14) * mm, "end": v(27.71, 46.76) * mm});
            skLineSegment(sketch, "E3.11.0.0", {"start": v(40.41, -42.14) * mm, "end": v(35.79, -42.14) * mm});
            skLineSegment(sketch, "E3.11.0.1", {"start": v(35.79, -46.76) * mm, "end": v(35.79, -42.14) * mm});
            skLineSegment(sketch, "E3.11.0.2", {"start": v(40.41, -46.76) * mm, "end": v(35.79, -46.76) * mm});
            skLineSegment(sketch, "E3.11.0.3", {"start": v(40.41, -46.76) * mm, "end": v(40.41, -42.14) * mm});
            skLineSegment(sketch, "E3.11.1.0", {"start": v(40.41, -29.44) * mm, "end": v(35.79, -29.44) * mm});
            skLineSegment(sketch, "E3.11.1.1", {"start": v(35.79, -34.06) * mm, "end": v(35.79, -29.44) * mm});
            skLineSegment(sketch, "E3.11.1.2", {"start": v(40.41, -34.06) * mm, "end": v(35.79, -34.06) * mm});
            skLineSegment(sketch, "E3.11.1.3", {"start": v(40.41, -34.06) * mm, "end": v(40.41, -29.44) * mm});
            skLineSegment(sketch, "E3.11.2.0", {"start": v(40.41, -16.74) * mm, "end": v(35.79, -16.74) * mm});
            skLineSegment(sketch, "E3.11.2.1", {"start": v(35.79, -21.36) * mm, "end": v(35.79, -16.74) * mm});
            skLineSegment(sketch, "E3.11.2.2", {"start": v(40.41, -21.36) * mm, "end": v(35.79, -21.36) * mm});
            skLineSegment(sketch, "E3.11.2.3", {"start": v(40.41, -21.36) * mm, "end": v(40.41, -16.74) * mm});
            skLineSegment(sketch, "E3.11.3.0", {"start": v(40.41, -4.04) * mm, "end": v(35.79, -4.04) * mm});
            skLineSegment(sketch, "E3.11.3.1", {"start": v(35.79, -8.66) * mm, "end": v(35.79, -4.04) * mm});
            skLineSegment(sketch, "E3.11.3.2", {"start": v(40.41, -8.66) * mm, "end": v(35.79, -8.66) * mm});
            skLineSegment(sketch, "E3.11.3.3", {"start": v(40.41, -8.66) * mm, "end": v(40.41, -4.04) * mm});
            skLineSegment(sketch, "E3.11.4.0", {"start": v(40.41, 8.66) * mm, "end": v(35.79, 8.66) * mm});
            skLineSegment(sketch, "E3.11.4.1", {"start": v(35.79, 4.04) * mm, "end": v(35.79, 8.66) * mm});
            skLineSegment(sketch, "E3.11.4.2", {"start": v(40.41, 4.04) * mm, "end": v(35.79, 4.04) * mm});
            skLineSegment(sketch, "E3.11.4.3", {"start": v(40.41, 4.04) * mm, "end": v(40.41, 8.66) * mm});
            skLineSegment(sketch, "E3.11.5.0", {"start": v(40.41, 21.36) * mm, "end": v(35.79, 21.36) * mm});
            skLineSegment(sketch, "E3.11.5.1", {"start": v(35.79, 16.74) * mm, "end": v(35.79, 21.36) * mm});
            skLineSegment(sketch, "E3.11.5.2", {"start": v(40.41, 16.74) * mm, "end": v(35.79, 16.74) * mm});
            skLineSegment(sketch, "E3.11.5.3", {"start": v(40.41, 16.74) * mm, "end": v(40.41, 21.36) * mm});
            skLineSegment(sketch, "E3.11.6.0", {"start": v(40.41, 34.06) * mm, "end": v(35.79, 34.06) * mm});
            skLineSegment(sketch, "E3.11.6.1", {"start": v(35.79, 29.44) * mm, "end": v(35.79, 34.06) * mm});
            skLineSegment(sketch, "E3.11.6.2", {"start": v(40.41, 29.44) * mm, "end": v(35.79, 29.44) * mm});
            skLineSegment(sketch, "E3.11.6.3", {"start": v(40.41, 29.44) * mm, "end": v(40.41, 34.06) * mm});
            skLineSegment(sketch, "E3.11.7.0", {"start": v(40.41, 46.76) * mm, "end": v(35.79, 46.76) * mm});
            skLineSegment(sketch, "E3.11.7.1", {"start": v(35.79, 42.14) * mm, "end": v(35.79, 46.76) * mm});
            skLineSegment(sketch, "E3.11.7.2", {"start": v(40.41, 42.14) * mm, "end": v(35.79, 42.14) * mm});
            skLineSegment(sketch, "E3.11.7.3", {"start": v(40.41, 42.14) * mm, "end": v(40.41, 46.76) * mm});
            skLineSegment(sketch, "E3.12.0.0", {"start": v(53.11, -42.14) * mm, "end": v(48.49, -42.14) * mm});
            skLineSegment(sketch, "E3.12.0.1", {"start": v(48.49, -46.76) * mm, "end": v(48.49, -42.14) * mm});
            skLineSegment(sketch, "E3.12.0.2", {"start": v(53.11, -46.76) * mm, "end": v(48.49, -46.76) * mm});
            skLineSegment(sketch, "E3.12.0.3", {"start": v(53.11, -46.76) * mm, "end": v(53.11, -42.14) * mm});
            skLineSegment(sketch, "E3.12.1.0", {"start": v(53.11, -29.44) * mm, "end": v(48.49, -29.44) * mm});
            skLineSegment(sketch, "E3.12.1.1", {"start": v(48.49, -34.06) * mm, "end": v(48.49, -29.44) * mm});
            skLineSegment(sketch, "E3.12.1.2", {"start": v(53.11, -34.06) * mm, "end": v(48.49, -34.06) * mm});
            skLineSegment(sketch, "E3.12.1.3", {"start": v(53.11, -34.06) * mm, "end": v(53.11, -29.44) * mm});
            skLineSegment(sketch, "E3.12.2.0", {"start": v(53.11, -16.74) * mm, "end": v(48.49, -16.74) * mm});
            skLineSegment(sketch, "E3.12.2.1", {"start": v(48.49, -21.36) * mm, "end": v(48.49, -16.74) * mm});
            skLineSegment(sketch, "E3.12.2.2", {"start": v(53.11, -21.36) * mm, "end": v(48.49, -21.36) * mm});
            skLineSegment(sketch, "E3.12.2.3", {"start": v(53.11, -21.36) * mm, "end": v(53.11, -16.74) * mm});
            skLineSegment(sketch, "E3.12.3.0", {"start": v(53.11, -4.04) * mm, "end": v(48.49, -4.04) * mm});
            skLineSegment(sketch, "E3.12.3.1", {"start": v(48.49, -8.66) * mm, "end": v(48.49, -4.04) * mm});
            skLineSegment(sketch, "E3.12.3.2", {"start": v(53.11, -8.66) * mm, "end": v(48.49, -8.66) * mm});
            skLineSegment(sketch, "E3.12.3.3", {"start": v(53.11, -8.66) * mm, "end": v(53.11, -4.04) * mm});
            skLineSegment(sketch, "E3.12.4.0", {"start": v(53.11, 8.66) * mm, "end": v(48.49, 8.66) * mm});
            skLineSegment(sketch, "E3.12.4.1", {"start": v(48.49, 4.04) * mm, "end": v(48.49, 8.66) * mm});
            skLineSegment(sketch, "E3.12.4.2", {"start": v(53.11, 4.04) * mm, "end": v(48.49, 4.04) * mm});
            skLineSegment(sketch, "E3.12.4.3", {"start": v(53.11, 4.04) * mm, "end": v(53.11, 8.66) * mm});
            skLineSegment(sketch, "E3.12.5.0", {"start": v(53.11, 21.36) * mm, "end": v(48.49, 21.36) * mm});
            skLineSegment(sketch, "E3.12.5.1", {"start": v(48.49, 16.74) * mm, "end": v(48.49, 21.36) * mm});
            skLineSegment(sketch, "E3.12.5.2", {"start": v(53.11, 16.74) * mm, "end": v(48.49, 16.74) * mm});
            skLineSegment(sketch, "E3.12.5.3", {"start": v(53.11, 16.74) * mm, "end": v(53.11, 21.36) * mm});
            skLineSegment(sketch, "E3.12.6.0", {"start": v(53.11, 34.06) * mm, "end": v(48.49, 34.06) * mm});
            skLineSegment(sketch, "E3.12.6.1", {"start": v(48.49, 29.44) * mm, "end": v(48.49, 34.06) * mm});
            skLineSegment(sketch, "E3.12.6.2", {"start": v(53.11, 29.44) * mm, "end": v(48.49, 29.44) * mm});
            skLineSegment(sketch, "E3.12.6.3", {"start": v(53.11, 29.44) * mm, "end": v(53.11, 34.06) * mm});
            skLineSegment(sketch, "E3.12.7.0", {"start": v(53.11, 46.76) * mm, "end": v(48.49, 46.76) * mm});
            skLineSegment(sketch, "E3.12.7.1", {"start": v(48.49, 42.14) * mm, "end": v(48.49, 46.76) * mm});
            skLineSegment(sketch, "E3.12.7.2", {"start": v(53.11, 42.14) * mm, "end": v(48.49, 42.14) * mm});
            skLineSegment(sketch, "E3.12.7.3", {"start": v(53.11, 42.14) * mm, "end": v(53.11, 46.76) * mm});
            skLineSegment(sketch, "E3.13.0.0", {"start": v(65.81, -42.14) * mm, "end": v(61.19, -42.14) * mm});
            skLineSegment(sketch, "E3.13.0.1", {"start": v(61.19, -46.76) * mm, "end": v(61.19, -42.14) * mm});
            skLineSegment(sketch, "E3.13.0.2", {"start": v(65.81, -46.76) * mm, "end": v(61.19, -46.76) * mm});
            skLineSegment(sketch, "E3.13.0.3", {"start": v(65.81, -46.76) * mm, "end": v(65.81, -42.14) * mm});
            skLineSegment(sketch, "E3.13.1.0", {"start": v(65.81, -29.44) * mm, "end": v(61.19, -29.44) * mm});
            skLineSegment(sketch, "E3.13.1.1", {"start": v(61.19, -34.06) * mm, "end": v(61.19, -29.44) * mm});
            skLineSegment(sketch, "E3.13.1.2", {"start": v(65.81, -34.06) * mm, "end": v(61.19, -34.06) * mm});
            skLineSegment(sketch, "E3.13.1.3", {"start": v(65.81, -34.06) * mm, "end": v(65.81, -29.44) * mm});
            skLineSegment(sketch, "E3.13.2.0", {"start": v(65.81, -16.74) * mm, "end": v(61.19, -16.74) * mm});
            skLineSegment(sketch, "E3.13.2.1", {"start": v(61.19, -21.36) * mm, "end": v(61.19, -16.74) * mm});
            skLineSegment(sketch, "E3.13.2.2", {"start": v(65.81, -21.36) * mm, "end": v(61.19, -21.36) * mm});
            skLineSegment(sketch, "E3.13.2.3", {"start": v(65.81, -21.36) * mm, "end": v(65.81, -16.74) * mm});
            skLineSegment(sketch, "E3.13.3.0", {"start": v(65.81, -4.04) * mm, "end": v(61.19, -4.04) * mm});
            skLineSegment(sketch, "E3.13.3.1", {"start": v(61.19, -8.66) * mm, "end": v(61.19, -4.04) * mm});
            skLineSegment(sketch, "E3.13.3.2", {"start": v(65.81, -8.66) * mm, "end": v(61.19, -8.66) * mm});
            skLineSegment(sketch, "E3.13.3.3", {"start": v(65.81, -8.66) * mm, "end": v(65.81, -4.04) * mm});
            skLineSegment(sketch, "E3.13.4.0", {"start": v(65.81, 8.66) * mm, "end": v(61.19, 8.66) * mm});
            skLineSegment(sketch, "E3.13.4.1", {"start": v(61.19, 4.04) * mm, "end": v(61.19, 8.66) * mm});
            skLineSegment(sketch, "E3.13.4.2", {"start": v(65.81, 4.04) * mm, "end": v(61.19, 4.04) * mm});
            skLineSegment(sketch, "E3.13.4.3", {"start": v(65.81, 4.04) * mm, "end": v(65.81, 8.66) * mm});
            skLineSegment(sketch, "E3.13.5.0", {"start": v(65.81, 21.36) * mm, "end": v(61.19, 21.36) * mm});
            skLineSegment(sketch, "E3.13.5.1", {"start": v(61.19, 16.74) * mm, "end": v(61.19, 21.36) * mm});
            skLineSegment(sketch, "E3.13.5.2", {"start": v(65.81, 16.74) * mm, "end": v(61.19, 16.74) * mm});
            skLineSegment(sketch, "E3.13.5.3", {"start": v(65.81, 16.74) * mm, "end": v(65.81, 21.36) * mm});
            skLineSegment(sketch, "E3.13.6.0", {"start": v(65.81, 34.06) * mm, "end": v(61.19, 34.06) * mm});
            skLineSegment(sketch, "E3.13.6.1", {"start": v(61.19, 29.44) * mm, "end": v(61.19, 34.06) * mm});
            skLineSegment(sketch, "E3.13.6.2", {"start": v(65.81, 29.44) * mm, "end": v(61.19, 29.44) * mm});
            skLineSegment(sketch, "E3.13.6.3", {"start": v(65.81, 29.44) * mm, "end": v(65.81, 34.06) * mm});
            skLineSegment(sketch, "E3.13.7.0", {"start": v(65.81, 46.76) * mm, "end": v(61.19, 46.76) * mm});
            skLineSegment(sketch, "E3.13.7.1", {"start": v(61.19, 42.14) * mm, "end": v(61.19, 46.76) * mm});
            skLineSegment(sketch, "E3.13.7.2", {"start": v(65.81, 42.14) * mm, "end": v(61.19, 42.14) * mm});
            skLineSegment(sketch, "E3.13.7.3", {"start": v(65.81, 42.14) * mm, "end": v(65.81, 46.76) * mm});
            skLineSegment(sketch, "E3.14.0.0", {"start": v(78.51, -42.14) * mm, "end": v(73.89, -42.14) * mm});
            skLineSegment(sketch, "E3.14.0.1", {"start": v(73.89, -46.76) * mm, "end": v(73.89, -42.14) * mm});
            skLineSegment(sketch, "E3.14.0.2", {"start": v(78.51, -46.76) * mm, "end": v(73.89, -46.76) * mm});
            skLineSegment(sketch, "E3.14.0.3", {"start": v(78.51, -46.76) * mm, "end": v(78.51, -42.14) * mm});
            skLineSegment(sketch, "E3.14.1.0", {"start": v(78.51, -29.44) * mm, "end": v(73.89, -29.44) * mm});
            skLineSegment(sketch, "E3.14.1.1", {"start": v(73.89, -34.06) * mm, "end": v(73.89, -29.44) * mm});
            skLineSegment(sketch, "E3.14.1.2", {"start": v(78.51, -34.06) * mm, "end": v(73.89, -34.06) * mm});
            skLineSegment(sketch, "E3.14.1.3", {"start": v(78.51, -34.06) * mm, "end": v(78.51, -29.44) * mm});
            skLineSegment(sketch, "E3.14.2.0", {"start": v(78.51, -16.74) * mm, "end": v(73.89, -16.74) * mm});
            skLineSegment(sketch, "E3.14.2.1", {"start": v(73.89, -21.36) * mm, "end": v(73.89, -16.74) * mm});
            skLineSegment(sketch, "E3.14.2.2", {"start": v(78.51, -21.36) * mm, "end": v(73.89, -21.36) * mm});
            skLineSegment(sketch, "E3.14.2.3", {"start": v(78.51, -21.36) * mm, "end": v(78.51, -16.74) * mm});
            skLineSegment(sketch, "E3.14.3.0", {"start": v(78.51, -4.04) * mm, "end": v(73.89, -4.04) * mm});
            skLineSegment(sketch, "E3.14.3.1", {"start": v(73.89, -8.66) * mm, "end": v(73.89, -4.04) * mm});
            skLineSegment(sketch, "E3.14.3.2", {"start": v(78.51, -8.66) * mm, "end": v(73.89, -8.66) * mm});
            skLineSegment(sketch, "E3.14.3.3", {"start": v(78.51, -8.66) * mm, "end": v(78.51, -4.04) * mm});
            skLineSegment(sketch, "E3.14.4.0", {"start": v(78.51, 8.66) * mm, "end": v(73.89, 8.66) * mm});
            skLineSegment(sketch, "E3.14.4.1", {"start": v(73.89, 4.04) * mm, "end": v(73.89, 8.66) * mm});
            skLineSegment(sketch, "E3.14.4.2", {"start": v(78.51, 4.04) * mm, "end": v(73.89, 4.04) * mm});
            skLineSegment(sketch, "E3.14.4.3", {"start": v(78.51, 4.04) * mm, "end": v(78.51, 8.66) * mm});
            skLineSegment(sketch, "E3.14.5.0", {"start": v(78.51, 21.36) * mm, "end": v(73.89, 21.36) * mm});
            skLineSegment(sketch, "E3.14.5.1", {"start": v(73.89, 16.74) * mm, "end": v(73.89, 21.36) * mm});
            skLineSegment(sketch, "E3.14.5.2", {"start": v(78.51, 16.74) * mm, "end": v(73.89, 16.74) * mm});
            skLineSegment(sketch, "E3.14.5.3", {"start": v(78.51, 16.74) * mm, "end": v(78.51, 21.36) * mm});
            skLineSegment(sketch, "E3.14.6.0", {"start": v(78.51, 34.06) * mm, "end": v(73.89, 34.06) * mm});
            skLineSegment(sketch, "E3.14.6.1", {"start": v(73.89, 29.44) * mm, "end": v(73.89, 34.06) * mm});
            skLineSegment(sketch, "E3.14.6.2", {"start": v(78.51, 29.44) * mm, "end": v(73.89, 29.44) * mm});
            skLineSegment(sketch, "E3.14.6.3", {"start": v(78.51, 29.44) * mm, "end": v(78.51, 34.06) * mm});
            skLineSegment(sketch, "E3.14.7.0", {"start": v(78.51, 46.76) * mm, "end": v(73.89, 46.76) * mm});
            skLineSegment(sketch, "E3.14.7.1", {"start": v(73.89, 42.14) * mm, "end": v(73.89, 46.76) * mm});
            skLineSegment(sketch, "E3.14.7.2", {"start": v(78.51, 42.14) * mm, "end": v(73.89, 42.14) * mm});
            skLineSegment(sketch, "E3.14.7.3", {"start": v(78.51, 42.14) * mm, "end": v(78.51, 46.76) * mm});
            skLineSegment(sketch, "E3.15.0.0", {"start": v(91.21, -42.14) * mm, "end": v(86.59, -42.14) * mm});
            skLineSegment(sketch, "E3.15.0.1", {"start": v(86.59, -46.76) * mm, "end": v(86.59, -42.14) * mm});
            skLineSegment(sketch, "E3.15.0.2", {"start": v(91.21, -46.76) * mm, "end": v(86.59, -46.76) * mm});
            skLineSegment(sketch, "E3.15.0.3", {"start": v(91.21, -46.76) * mm, "end": v(91.21, -42.14) * mm});
            skLineSegment(sketch, "E3.15.1.0", {"start": v(91.21, -29.44) * mm, "end": v(86.59, -29.44) * mm});
            skLineSegment(sketch, "E3.15.1.1", {"start": v(86.59, -34.06) * mm, "end": v(86.59, -29.44) * mm});
            skLineSegment(sketch, "E3.15.1.2", {"start": v(91.21, -34.06) * mm, "end": v(86.59, -34.06) * mm});
            skLineSegment(sketch, "E3.15.1.3", {"start": v(91.21, -34.06) * mm, "end": v(91.21, -29.44) * mm});
            skLineSegment(sketch, "E3.15.2.0", {"start": v(91.21, -16.74) * mm, "end": v(86.59, -16.74) * mm});
            skLineSegment(sketch, "E3.15.2.1", {"start": v(86.59, -21.36) * mm, "end": v(86.59, -16.74) * mm});
            skLineSegment(sketch, "E3.15.2.2", {"start": v(91.21, -21.36) * mm, "end": v(86.59, -21.36) * mm});
            skLineSegment(sketch, "E3.15.2.3", {"start": v(91.21, -21.36) * mm, "end": v(91.21, -16.74) * mm});
            skLineSegment(sketch, "E3.15.3.0", {"start": v(91.21, -4.04) * mm, "end": v(86.59, -4.04) * mm});
            skLineSegment(sketch, "E3.15.3.1", {"start": v(86.59, -8.66) * mm, "end": v(86.59, -4.04) * mm});
            skLineSegment(sketch, "E3.15.3.2", {"start": v(91.21, -8.66) * mm, "end": v(86.59, -8.66) * mm});
            skLineSegment(sketch, "E3.15.3.3", {"start": v(91.21, -8.66) * mm, "end": v(91.21, -4.04) * mm});
            skLineSegment(sketch, "E3.15.4.0", {"start": v(91.21, 8.66) * mm, "end": v(86.59, 8.66) * mm});
            skLineSegment(sketch, "E3.15.4.1", {"start": v(86.59, 4.04) * mm, "end": v(86.59, 8.66) * mm});
            skLineSegment(sketch, "E3.15.4.2", {"start": v(91.21, 4.04) * mm, "end": v(86.59, 4.04) * mm});
            skLineSegment(sketch, "E3.15.4.3", {"start": v(91.21, 4.04) * mm, "end": v(91.21, 8.66) * mm});
            skLineSegment(sketch, "E3.15.5.0", {"start": v(91.21, 21.36) * mm, "end": v(86.59, 21.36) * mm});
            skLineSegment(sketch, "E3.15.5.1", {"start": v(86.59, 16.74) * mm, "end": v(86.59, 21.36) * mm});
            skLineSegment(sketch, "E3.15.5.2", {"start": v(91.21, 16.74) * mm, "end": v(86.59, 16.74) * mm});
            skLineSegment(sketch, "E3.15.5.3", {"start": v(91.21, 16.74) * mm, "end": v(91.21, 21.36) * mm});
            skLineSegment(sketch, "E3.15.6.0", {"start": v(91.21, 34.06) * mm, "end": v(86.59, 34.06) * mm});
            skLineSegment(sketch, "E3.15.6.1", {"start": v(86.59, 29.44) * mm, "end": v(86.59, 34.06) * mm});
            skLineSegment(sketch, "E3.15.6.2", {"start": v(91.21, 29.44) * mm, "end": v(86.59, 29.44) * mm});
            skLineSegment(sketch, "E3.15.6.3", {"start": v(91.21, 29.44) * mm, "end": v(91.21, 34.06) * mm});
            skLineSegment(sketch, "E3.15.7.0", {"start": v(91.21, 46.76) * mm, "end": v(86.59, 46.76) * mm});
            skLineSegment(sketch, "E3.15.7.1", {"start": v(86.59, 42.14) * mm, "end": v(86.59, 46.76) * mm});
            skLineSegment(sketch, "E3.15.7.2", {"start": v(91.21, 42.14) * mm, "end": v(86.59, 42.14) * mm});
            skLineSegment(sketch, "E3.15.7.3", {"start": v(91.21, 42.14) * mm, "end": v(91.21, 46.76) * mm});
            skLineSegment(sketch, "E3.16.0.0", {"start": v(103.91, -42.14) * mm, "end": v(99.29, -42.14) * mm});
            skLineSegment(sketch, "E3.16.0.1", {"start": v(99.29, -46.76) * mm, "end": v(99.29, -42.14) * mm});
            skLineSegment(sketch, "E3.16.0.2", {"start": v(103.91, -46.76) * mm, "end": v(99.29, -46.76) * mm});
            skLineSegment(sketch, "E3.16.0.3", {"start": v(103.91, -46.76) * mm, "end": v(103.91, -42.14) * mm});
            skLineSegment(sketch, "E3.16.1.0", {"start": v(103.91, -29.44) * mm, "end": v(99.29, -29.44) * mm});
            skLineSegment(sketch, "E3.16.1.1", {"start": v(99.29, -34.06) * mm, "end": v(99.29, -29.44) * mm});
            skLineSegment(sketch, "E3.16.1.2", {"start": v(103.91, -34.06) * mm, "end": v(99.29, -34.06) * mm});
            skLineSegment(sketch, "E3.16.1.3", {"start": v(103.91, -34.06) * mm, "end": v(103.91, -29.44) * mm});
            skLineSegment(sketch, "E3.16.2.0", {"start": v(103.91, -16.74) * mm, "end": v(99.29, -16.74) * mm});
            skLineSegment(sketch, "E3.16.2.1", {"start": v(99.29, -21.36) * mm, "end": v(99.29, -16.74) * mm});
            skLineSegment(sketch, "E3.16.2.2", {"start": v(103.91, -21.36) * mm, "end": v(99.29, -21.36) * mm});
            skLineSegment(sketch, "E3.16.2.3", {"start": v(103.91, -21.36) * mm, "end": v(103.91, -16.74) * mm});
            skLineSegment(sketch, "E3.16.3.0", {"start": v(103.91, -4.04) * mm, "end": v(99.29, -4.04) * mm});
            skLineSegment(sketch, "E3.16.3.1", {"start": v(99.29, -8.66) * mm, "end": v(99.29, -4.04) * mm});
            skLineSegment(sketch, "E3.16.3.2", {"start": v(103.91, -8.66) * mm, "end": v(99.29, -8.66) * mm});
            skLineSegment(sketch, "E3.16.3.3", {"start": v(103.91, -8.66) * mm, "end": v(103.91, -4.04) * mm});
            skLineSegment(sketch, "E3.16.4.0", {"start": v(103.91, 8.66) * mm, "end": v(99.29, 8.66) * mm});
            skLineSegment(sketch, "E3.16.4.1", {"start": v(99.29, 4.04) * mm, "end": v(99.29, 8.66) * mm});
            skLineSegment(sketch, "E3.16.4.2", {"start": v(103.91, 4.04) * mm, "end": v(99.29, 4.04) * mm});
            skLineSegment(sketch, "E3.16.4.3", {"start": v(103.91, 4.04) * mm, "end": v(103.91, 8.66) * mm});
            skLineSegment(sketch, "E3.16.5.0", {"start": v(103.91, 21.36) * mm, "end": v(99.29, 21.36) * mm});
            skLineSegment(sketch, "E3.16.5.1", {"start": v(99.29, 16.74) * mm, "end": v(99.29, 21.36) * mm});
            skLineSegment(sketch, "E3.16.5.2", {"start": v(103.91, 16.74) * mm, "end": v(99.29, 16.74) * mm});
            skLineSegment(sketch, "E3.16.5.3", {"start": v(103.91, 16.74) * mm, "end": v(103.91, 21.36) * mm});
            skLineSegment(sketch, "E3.16.6.0", {"start": v(103.91, 34.06) * mm, "end": v(99.29, 34.06) * mm});
            skLineSegment(sketch, "E3.16.6.1", {"start": v(99.29, 29.44) * mm, "end": v(99.29, 34.06) * mm});
            skLineSegment(sketch, "E3.16.6.2", {"start": v(103.91, 29.44) * mm, "end": v(99.29, 29.44) * mm});
            skLineSegment(sketch, "E3.16.6.3", {"start": v(103.91, 29.44) * mm, "end": v(103.91, 34.06) * mm});
            skLineSegment(sketch, "E3.16.7.0", {"start": v(103.91, 46.76) * mm, "end": v(99.29, 46.76) * mm});
            skLineSegment(sketch, "E3.16.7.1", {"start": v(99.29, 42.14) * mm, "end": v(99.29, 46.76) * mm});
            skLineSegment(sketch, "E3.16.7.2", {"start": v(103.91, 42.14) * mm, "end": v(99.29, 42.14) * mm});
            skLineSegment(sketch, "E3.16.7.3", {"start": v(103.91, 42.14) * mm, "end": v(103.91, 46.76) * mm});
            skLineSegment(sketch, "E3.direction1", {"start": v(-103.91, -42.14) * mm, "end": v(-91.21, -42.14) * mm, "construction": true});
            skLineSegment(sketch, "E3.direction2", {"start": v(-103.91, -42.14) * mm, "end": v(-103.91, -29.44) * mm, "construction": true});
            skSolve(sketch);
        }
        {
            var Q0;
            Q0=makeQuery(id+"F0.imprint","IMPRINT",FACE,{"disambiguationData":[TD([[makeQuery(id+"F0.imprint","IMPRINT",EDGE,{"derivedFrom":sQuery(id+"F0.wireOp",EDGE,"E0.bottom")}),1.0]])]});
            extrude(context, id + "F1", {"entities" : qUnion([Q0]), "depth" : 1 / 203.2 * mm});
        }
    });
